# Revit family: Sanitary_Toilets_Sanindusa_Look-F-D-Close-Coupled-Toilet
name_source: partatom
category: Plumbing Fixtures
revit_build: Autodesk Revit 2018 (Build: 20170223_1515(x64)
units: mm (PartAtom-declared; Revit-internal decimal feet)

## family parameters
Always vertical = Yes
Cut with Voids When Loaded = No
Host = Wall
OmniClass Number = 23.45.00.00
OmniClass Title = Sanitary, Laundry, and Cleaning Equipment
Part Type = Normal
Room Calculation Point = No
Round Connector Dimension = Use Diameter
Shared = No

## types (1)
- SANINDUSA_FDclosecoupledtoilet_134021004_350x630x397_Look
    AssetType = Fixed
    CodePerformance = EN 997:2012 CL 1 - 6 A
    Color = White
    Constituents = Compatible toilet seats (not included): 2341100-Look toilet seat with clipoff system; 2343100-Look toilet seat with clipoff and slowclose system. Compatible cisterns (not included): 134111004LM - Look bottom water supply connection cistern with dual flush mechanism; 134113004LM - Look side water supply connection cistern with dual flush mechanism. 24-fixing kit (included)
    Cost = 0 $
    Description = Soil appliance for the disposal of excrement.
    DrainSize = 90 mm  [stored 0.295276 ft]
    Edition number = 1
    Features = Domestic and commercial use. Versatile timeless design. Seats with clipoff system easy to clean and slow close option. Back to wall WC. Extensive range of washbasins to combine.
    Finish = gloss
    InletDiameter = 50 mm
    Installation Instructions = https://www.tec.sanindusa.pt
    InstallationDate = 1900-12-31T23:59:59
    ManufacturerName = Sanindusa
    ManufacturerURL = www.tec.sanindusa.pt
    Material = Vitreous China
    ModelNumber = 134021004
    ModelReference = Look
    Name = Look F|D close coupled toilet
    NominalHeight = 397 mm
    NominalLength = 350 mm
    NominalWidth = 630 mm
    Product Guid = ce2b25a5-fa19-49a6-b23b-5ad46306750d
    Product data url = https://bimobject.com
    ProductInformation = https://www.tec.sanindusa.pt
    ProductionYear = 2018
    Size = 350x630x397
    SustainabilityPerformance = n/a
n/a
    URL = www.tec.sanindusa.pt
    Uniclass2015Code = Pr_40_20_93_94
    Uniclass2015Title = WC pans
    Uniclass2015Version = Products v1.6
    Version = 1
    WarrantyDescription = https://www.tec.sanindusa.pt
    WarrantyDurationParts = 5
    WarrantyDurationUnit = year
    WarrantyStartDate = 1900-12-31T23:59:59
    Weight = 30.10 kg

note: [stored X ft] marks values corroborated as IEEE doubles in the binary element streams (Revit-internal decimal feet)

## geometry (parser evidence)
native form markers: Sweep x7
no freeform markers — native parametric forms only
